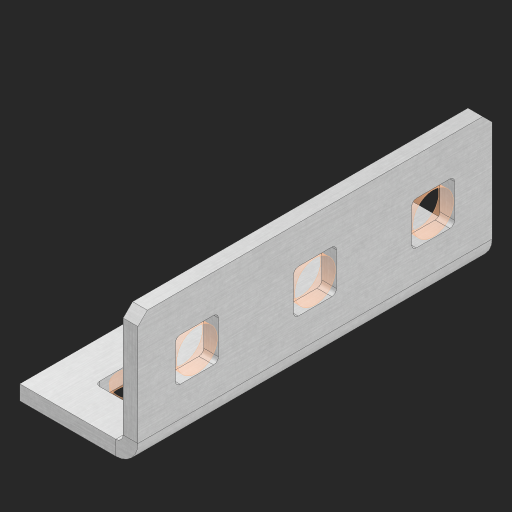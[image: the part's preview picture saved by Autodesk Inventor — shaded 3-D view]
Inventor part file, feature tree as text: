
AUTODESK INVENTOR PART (.ipt)
format: ipt  version: 2023 (Build 270158000, 158)  size: 473,088 bytes
history: native  units: in
note: dims shown in document units (in); Inventor stores cm internally (conversion verified against a paired STEP export)
features: other x11, sheet_metal_op x10, sketch x8, extrude x5, mirror x1, pattern_linear x1, chamfer x1
ambient origin geometry x8: Origin, YZ Plane, XZ Plane, XY Plane, X Axis, Y Axis, Z Axis, Center Point
bodies: Solid1 (feature_tree), Body (feature_tree)
feature tree (37):
  other  "Flange Pattern Plane"
  sheet_metal_op  "Flange Pattern"
  sheet_metal_op  "Body Pattern"
  other  "Arc Length"
  mirror  "Notch Mirror"
  pattern_linear  "Notch Pattern"  Spacing1=0.25in  [1 undecoded]
  chamfer  "End Chamfer"
  extrude  "Half Cut"  Depth=0.0625in
  sketch  "Sketch1"  dims[d0=1.5in]
  other  "Plate1"
  sketch  "Sketch2"  dims[d1=1.5in]
  other  "Plate2"
  sheet_metal_op  "Bend1"
  sheet_metal_op  "Corner1"
  sketch  "Sketch3"  dims[d2=0.0625in]
  other  "Flange Pattern Sketch"
  sketch  "Sketch7"  dims[d3=0.0625in]
  other  "Srf1"
  other  "Srf2"
  sketch  "Sketch8"  dims[d4=0.0312in]
  sketch  "Sketch9"  dims[d5=0.125in]
  other  "Srf91"
  sheet_metal_op  "Body Pattern Sketch"
  other  "Srf92"
  sketch  "Sketch13"  dims[d6=0.0625in]
  sketch  "Sketch14"  dims[d7=0.5in d8=90.0deg d9=0.0312in d10=0.25in d11=0.0625in d12=0.0625in d16=0.182in d17=0.02in d18=0.0625in d19=0.0in d20=0.25in d21=0.25in d46=0.172in d47=1.0in d48=0.0in d49=0.182in d50=0.02in d51=0.25in d52=0.25in d53=0.0625in d54=0.0in d55=0.172in d56=1.0in d57=0.0in d60=1.1811in d62=0.5in d63=0.3937in d65=0.5in d85=0.1473in d86=0.1782in d88=0.04in d89=0.0625in d90=0.0in d91=0.04in d92=0.0491in d95=2.5in d96=0.04in d97=0.25in d98=45.0deg d101=0.0in d102=2.497in d131=0.5in d132=1.1811in d134=0.5in d139=0.5in]
  other  "Srf856"
  other  "Srf1310"
  sheet_metal_op  "Flange Stamp"
  sheet_metal_op  "Flange Circle"
  sheet_metal_op  "Body Stamp"
  sheet_metal_op  "Body Circle"
  sheet_metal_op  "Notch"
  extrude  "ExtrusionSrf2"  Depth=0.0625in
  extrude  "ExtrusionSrf92"  Depth=0.182in
  extrude  "ExtrusionSrf856"  Depth=0.02in
  extrude  "ExtrusionSrf1310"  Depth=0.0625in
note: 1 required parameter value undecoded (feature->parameter linkage not recoverable at this tier; creation-order binding heuristic only, values carry confidence <= 0.55)
